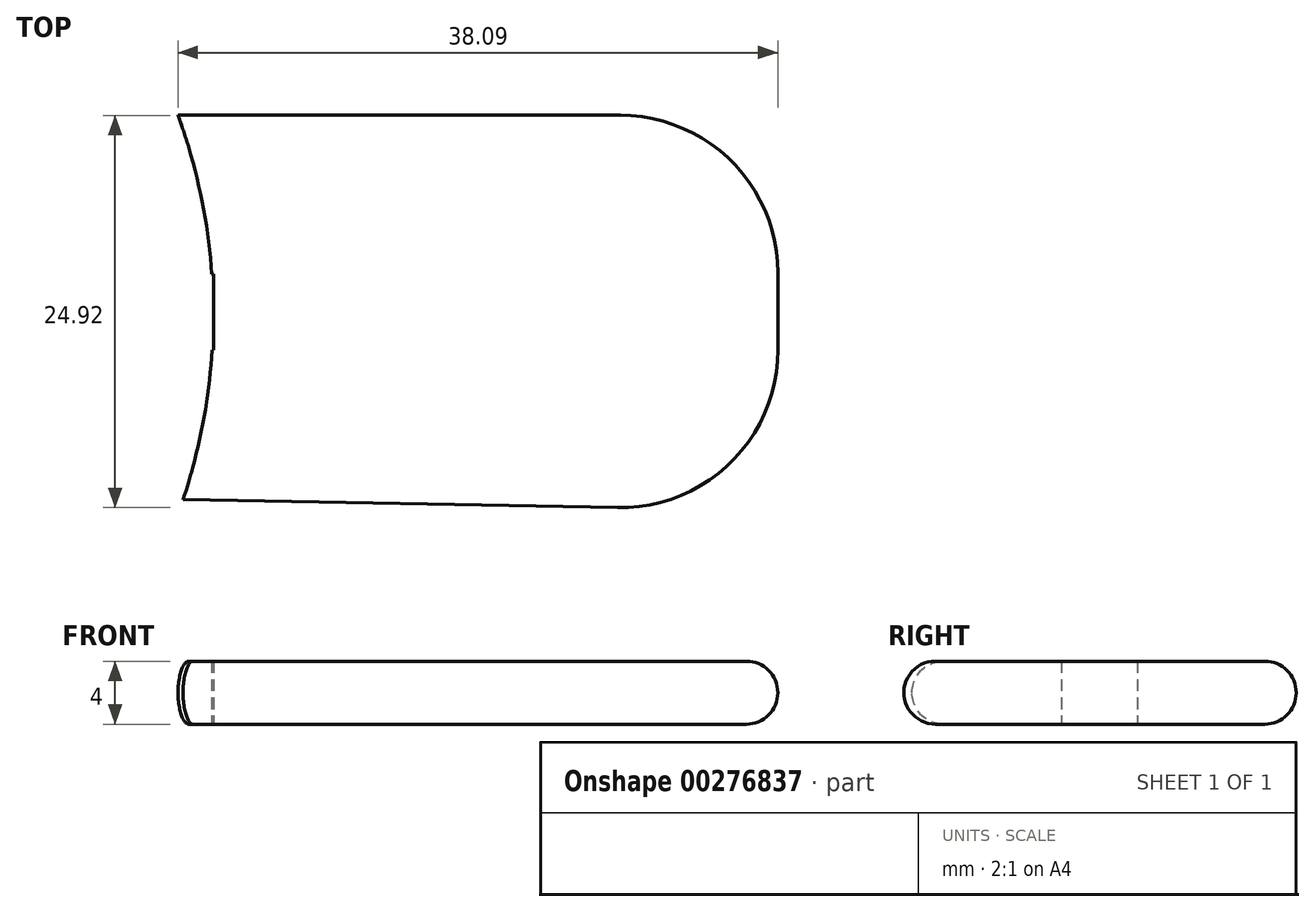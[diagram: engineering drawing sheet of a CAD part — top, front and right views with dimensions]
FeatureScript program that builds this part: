
annotation { "Feature Type Name" : "Feature", "Feature Type Description" : "" }
export const myFeature = defineFeature(function(context is Context, id is Id, definition is map)
    precondition{}
    {
        {
            var Q0;
            Q0=qCreatedBy(makeId("Top.planeOp"),FACE);
            var sketch = newSketch(context, id + "F0", { "sketchPlane" : qUnion([Q0])});
            skArc(sketch, "E0", {"start": v(35.09, -11.74) * mm, "mid": v(36.32, -7.07) * mm, "end": v(36.93, -2.27) * mm});
            skLineSegment(sketch, "E1", {"start": v(34.77, 12.65) * mm, "end": v(34.77, 12.65) * mm});
            skLineSegment(sketch, "E2", {"start": v(72.86, 2.65) * mm, "end": v(72.86, -2.27) * mm});
            skLineSegment(sketch, "E3", {"start": v(62.67, -12.26) * mm, "end": v(35.09, -11.74) * mm});
            skPoint(sketch, "E4.visualSharp", {"position": v(72.86, 12.65) * mm});
            skArc(sketch, "E4.filletArc", {"start": v(72.86, 2.65) * mm, "mid": v(69.93, 9.72) * mm, "end": v(62.86, 12.65) * mm});
            skPoint(sketch, "E5.visualSharp", {"position": v(72.86, -12.46) * mm});
            skArc(sketch, "E5.filletArc", {"start": v(62.67, -12.26) * mm, "mid": v(69.87, -9.4) * mm, "end": v(72.86, -2.27) * mm});
            skLineSegment(sketch, "E6", {"start": v(34.77, 12.65) * mm, "end": v(62.86, 12.65) * mm});
            skLineSegment(sketch, "E7.top", {"start": v(72.86, 2.58) * mm, "end": v(72.86, 2.58) * mm});
            skLineSegment(sketch, "E7.left", {"start": v(72.86, -2.27) * mm, "end": v(72.86, 2.58) * mm});
            skLineSegment(sketch, "E7.right", {"start": v(37, -2.27) * mm, "end": v(37, 2.58) * mm});
            skLineSegment(sketch, "E8.trimOffspring", {"start": v(37, -2.27) * mm, "end": v(36.93, -2.27) * mm});
            skLineSegment(sketch, "E9.trimOffspring", {"start": v(37, 2.58) * mm, "end": v(36.91, 2.58) * mm});
            skArc(sketch, "E10.trimOffspring", {"start": v(36.91, 2.58) * mm, "mid": v(36.2, 7.69) * mm, "end": v(34.77, 12.65) * mm});
            skSolve(sketch);
        }
        {
            var Q0;
            Q0=makeQuery(id+"F0.imprint","IMPRINT",FACE,{"disambiguationData":[TD([[makeQuery(id+"F0.imprint","IMPRINT",EDGE,{"derivedFrom":sQuery(id+"F0.wireOp",EDGE,"E0")}),-1.0]])]});
            extrude(context, id + "F1", {"entities" : qUnion([Q0]), "endBound" : BoundingType.SYMMETRIC, "depth" : 4 * mm});
        }
        {
            var Q0;
            Q0=makeQuery(id+"F1.opExtrude","CAP_EDGE",EDGE,{"disambiguationData":[OSD([sQuery(id+"F0.wireOp",EDGE,"E3")])],"isStart":true});
            fillet(context, id + "F2", {"entities" : qUnion([Q0]), "radius" : 2 * mm, "tangentPropagation" : true, "allowEdgeOverflow" : false});
        }
        {
            var Q0;
            Q0=makeQuery(id+"F1.opExtrude","CAP_EDGE",EDGE,{"disambiguationData":[OSD([sQuery(id+"F0.wireOp",EDGE,"E4.filletArc")])],"isStart":false});
            fillet(context, id + "F3", {"entities" : qUnion([Q0]), "radius" : 2 * mm, "tangentPropagation" : true, "allowEdgeOverflow" : false});
        }
    });
